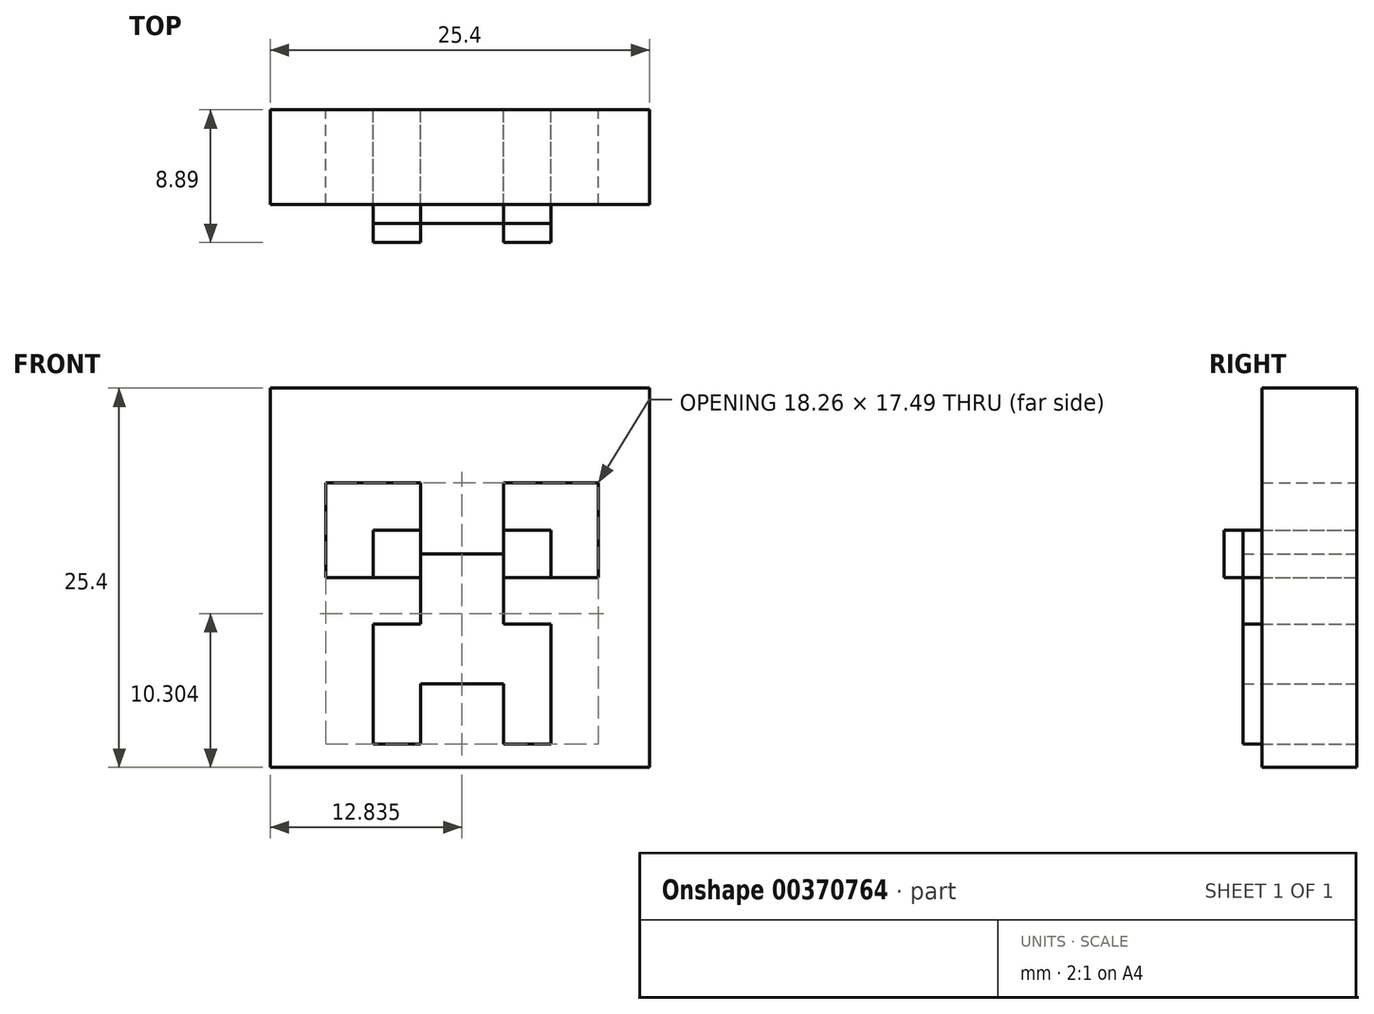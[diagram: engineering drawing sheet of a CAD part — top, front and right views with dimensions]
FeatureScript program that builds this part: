
annotation { "Feature Type Name" : "Feature", "Feature Type Description" : "" }
export const myFeature = defineFeature(function(context is Context, id is Id, definition is map)
    precondition{}
    {
        {
            var Q0;
            Q0=qCreatedBy(makeId("Front.planeOp"),FACE);
            var sketch = newSketch(context, id + "F0", { "sketchPlane" : qUnion([Q0])});
            skLineSegment(sketch, "E0.bottom", {"start": v(12.7, -12.7) * mm, "end": v(-12.7, -12.7) * mm});
            skLineSegment(sketch, "E0.top", {"start": v(12.7, 12.7) * mm, "end": v(-12.7, 12.7) * mm});
            skLineSegment(sketch, "E0.left", {"start": v(12.7, -12.7) * mm, "end": v(12.7, 12.7) * mm});
            skLineSegment(sketch, "E0.right", {"start": v(-12.7, -12.7) * mm, "end": v(-12.7, 12.7) * mm});
            skLineSegment(sketch, "E1.bottom", {"start": v(-2.65, 0) * mm, "end": v(-9, 0) * mm});
            skLineSegment(sketch, "E1.top", {"start": v(-2.65, 6.35) * mm, "end": v(-9, 6.35) * mm});
            skLineSegment(sketch, "E1.left", {"start": v(-2.65, 0) * mm, "end": v(-2.65, 6.35) * mm});
            skLineSegment(sketch, "E1.right", {"start": v(-9, 0) * mm, "end": v(-9, 6.35) * mm});
            skPoint(sketch, "E1.middle", {"position": v(-5.82, 3.18) * mm});
            skLineSegment(sketch, "E2.bottom", {"start": v(9.27, 0) * mm, "end": v(2.92, 0) * mm});
            skLineSegment(sketch, "E2.top", {"start": v(9.27, 6.35) * mm, "end": v(2.92, 6.35) * mm});
            skLineSegment(sketch, "E2.left", {"start": v(9.27, 0) * mm, "end": v(9.27, 6.35) * mm});
            skLineSegment(sketch, "E2.right", {"start": v(2.92, 0) * mm, "end": v(2.92, 6.35) * mm});
            skPoint(sketch, "E2.middle", {"position": v(6.1, 3.18) * mm});
            skLineSegment(sketch, "E3.left", {"start": v(-2.65, 0) * mm, "end": v(-2.65, -3.08) * mm});
            skLineSegment(sketch, "E3.right", {"start": v(2.92, 0) * mm, "end": v(2.92, -3.08) * mm});
            skLineSegment(sketch, "E4", {"start": v(-2.65, -3.08) * mm, "end": v(-5.82, -3.08) * mm});
            skLineSegment(sketch, "E5", {"start": v(-5.82, -3.08) * mm, "end": v(-5.82, -11.14) * mm});
            skLineSegment(sketch, "E6", {"start": v(-5.82, -11.14) * mm, "end": v(-2.65, -11.14) * mm});
            skLineSegment(sketch, "E7", {"start": v(-2.65, -11.14) * mm, "end": v(-2.65, -7.11) * mm});
            skLineSegment(sketch, "E8", {"start": v(2.92, -3.08) * mm, "end": v(6.1, -3.08) * mm});
            skPoint(sketch, "E8.endSnap0", {"position": v(6.1, 0) * mm});
            skLineSegment(sketch, "E9", {"start": v(6.1, -3.08) * mm, "end": v(6.1, -11.14) * mm});
            skLineSegment(sketch, "E10", {"start": v(6.1, -11.14) * mm, "end": v(2.92, -11.14) * mm});
            skLineSegment(sketch, "E11", {"start": v(2.92, -11.14) * mm, "end": v(2.92, -7.11) * mm});
            skLineSegment(sketch, "E12", {"start": v(-2.65, -7.11) * mm, "end": v(2.92, -7.11) * mm});
            skLineSegment(sketch, "E13.bottom", {"start": v(-5.82, 3.18) * mm, "end": v(-2.65, 3.18) * mm});
            skLineSegment(sketch, "E13.top", {"start": v(-5.82, 0) * mm, "end": v(-2.65, 0) * mm});
            skLineSegment(sketch, "E13.left", {"start": v(-5.82, 3.18) * mm, "end": v(-5.82, 0) * mm});
            skLineSegment(sketch, "E13.right", {"start": v(-2.65, 3.18) * mm, "end": v(-2.65, 0) * mm});
            skLineSegment(sketch, "E14.bottom", {"start": v(6.1, 3.18) * mm, "end": v(2.92, 3.18) * mm});
            skLineSegment(sketch, "E14.top", {"start": v(6.1, 0) * mm, "end": v(2.92, 0) * mm});
            skLineSegment(sketch, "E14.left", {"start": v(6.1, 3.18) * mm, "end": v(6.1, 0) * mm});
            skLineSegment(sketch, "E14.right", {"start": v(2.92, 3.18) * mm, "end": v(2.92, 0) * mm});
            skLineSegment(sketch, "E15", {"start": v(-2.65, 1.59) * mm, "end": v(2.92, 1.59) * mm});
            skSolve(sketch);
        }
        {
            var Q0;
            Q0=makeQuery(id+"F0.imprint","IMPRINT",FACE,{"disambiguationData":[TD([[makeQuery(id+"F0.imprint","IMPRINT",EDGE,{"derivedFrom":sQuery(id+"F0.wireOp",EDGE,"E3.bottom")}),-1.0]])]});
            var Q1;
            Q1=makeQuery(id+"F0.imprint","IMPRINT",FACE,{"disambiguationData":[TD([[makeQuery(id+"F0.imprint","IMPRINT",EDGE,{"derivedFrom":sQuery(id+"F0.wireOp",EDGE,"E1.bottom")}),-1.0]])]});
            var Q2;
            Q2=makeQuery(id+"F0.imprint","IMPRINT",FACE,{"disambiguationData":[TD([[makeQuery(id+"F0.imprint","IMPRINT",EDGE,{"derivedFrom":sQuery(id+"F0.wireOp",EDGE,"E2.bottom")}),-1.0]])]});
            extrude(context, id + "F1", {"entities" : qUnion([Q0, Q1, Q2]), "depth" : 7.62 * mm});
        }
        {
            var Q0;
            Q0=makeQuery(id+"F0.imprint","IMPRINT",FACE,{"disambiguationData":[TD([[makeQuery(id+"F0.imprint","IMPRINT",EDGE,{"derivedFrom":sQuery(id+"F0.wireOp",EDGE,"E13.bottom")}),-1.0]])]});
            var Q1;
            Q1=makeQuery(id+"F0.imprint","IMPRINT",FACE,{"disambiguationData":[TD([[makeQuery(id+"F0.imprint","IMPRINT",EDGE,{"derivedFrom":sQuery(id+"F0.wireOp",EDGE,"E14.bottom")}),1.0]])]});
            extrude(context, id + "F2", {"entities" : qUnion([Q0, Q1]), "depth" : 8.9 * mm});
        }
        {
            var Q0;
            {var subQ0=sQuery(id+"F0.wireOp",EDGE,"E3.left");Q0=makeQuery(id+"F0.imprint","IMPRINT",FACE,{"disambiguationData":[TD([[makeQuery(id+"F0.imprint","IMPRINT",EDGE,{"derivedFrom":subQ0}),1.0]])]});}
            extrude(context, id + "F3", {"entities" : qUnion([Q0]), "depth" : 7.62 * mm});
        }
        {
            var Q0;
            Q0=makeQuery(id+"F0.imprint","IMPRINT",FACE,{"disambiguationData":[TD([[makeQuery(id+"F0.imprint","IMPRINT",EDGE,{"derivedFrom":sQuery(id+"F0.wireOp",EDGE,"E0.bottom")}),-1.0]])]});
            extrude(context, id + "F4", {"entities" : qUnion([Q0]), "depth" : 6.35 * mm});
        }
    });
